annotation { "Feature Type Name" : "Feature", "Feature Type Description" : "" }
export const myFeature = defineFeature(function(context is Context, id is Id, definition is map)
    precondition{}
    {
        {
            var Q0;
            Q0=qCreatedBy(makeId("Right.planeOp"),FACE);
            var sketch = newSketch(context, id + "F0", { "sketchPlane" : qUnion([Q0])});
            skLineSegment(sketch, "E0", {"start": v(0, 0) * mm, "end": v(-381, 0) * mm});
            skLineSegment(sketch, "E1", {"start": v(0, 0) * mm, "end": v(381, 0) * mm});
            skLineSegment(sketch, "E2", {"start": v(0, 0) * mm, "end": v(0, 190.5) * mm});
            skLineSegment(sketch, "E3", {"start": v(0, 190.5) * mm, "end": v(0, 228.6) * mm});
            skLineSegment(sketch, "E4", {"start": v(381, 0) * mm, "end": v(457.2, 0) * mm});
            skLineSegment(sketch, "E5", {"start": v(-381, 0) * mm, "end": v(-457.2, 0) * mm});
            skLineSegment(sketch, "E6", {"start": v(-457.2, 0) * mm, "end": v(0, 228.6) * mm});
            skLineSegment(sketch, "E7", {"start": v(457.2, 0) * mm, "end": v(0, 228.6) * mm});
            skLineSegment(sketch, "E8", {"start": v(381, 0) * mm, "end": v(0, 190.5) * mm});
            skLineSegment(sketch, "E9", {"start": v(-381, 0) * mm, "end": v(0, 190.5) * mm});
            skLineSegment(sketch, "E10", {"start": v(-381, 0) * mm, "end": v(-381, -279.4) * mm});
            skLineSegment(sketch, "E11", {"start": v(-381, -279.4) * mm, "end": v(-381, -330.2) * mm});
            skLineSegment(sketch, "E12", {"start": v(381, 0) * mm, "end": v(381, -279.4) * mm});
            skLineSegment(sketch, "E13", {"start": v(-381, -279.4) * mm, "end": v(381, -279.4) * mm});
            skLineSegment(sketch, "E14", {"start": v(381, -279.4) * mm, "end": v(381, -330.2) * mm});
            skLineSegment(sketch, "E15", {"start": v(381, -330.2) * mm, "end": v(-381, -330.2) * mm});
            skLineSegment(sketch, "E16", {"start": v(381, -279.4) * mm, "end": v(762, -279.4) * mm});
            skLineSegment(sketch, "E17", {"start": v(381, -330.2) * mm, "end": v(762, -330.2) * mm});
            skLineSegment(sketch, "E18", {"start": v(762, -330.2) * mm, "end": v(762, -279.4) * mm});
            skLineSegment(sketch, "E19", {"start": v(762, -279.4) * mm, "end": v(762, -50.8) * mm});
            skLineSegment(sketch, "E20", {"start": v(381, 0) * mm, "end": v(762, -50.8) * mm});
            skLineSegment(sketch, "E21", {"start": v(381, 0) * mm, "end": v(381, -50.8) * mm});
            skLineSegment(sketch, "E22", {"start": v(762, -50.8) * mm, "end": v(762, -101.6) * mm});
            skLineSegment(sketch, "E23", {"start": v(762, -101.6) * mm, "end": v(381, -50.8) * mm});
            skLineSegment(sketch, "E24", {"start": v(-279.4, -279.4) * mm, "end": v(-279.4, -101.6) * mm});
            skLineSegment(sketch, "E25", {"start": v(-279.4, -101.6) * mm, "end": v(-203.2, -101.6) * mm});
            skLineSegment(sketch, "E26", {"start": v(-203.2, -101.6) * mm, "end": v(-203.2, -279.4) * mm});
            skLineSegment(sketch, "E27.bottom", {"start": v(50.8, -101.6) * mm, "end": v(279.4, -101.6) * mm});
            skLineSegment(sketch, "E27.top", {"start": v(50.8, -203.2) * mm, "end": v(279.4, -203.2) * mm});
            skLineSegment(sketch, "E27.left", {"start": v(50.8, -101.6) * mm, "end": v(50.8, -203.2) * mm});
            skLineSegment(sketch, "E27.right", {"start": v(279.4, -101.6) * mm, "end": v(279.4, -203.2) * mm});
            skLineSegment(sketch, "E28.0", {"start": v(63.5, -190.5) * mm, "end": v(266.7, -190.5) * mm});
            skLineSegment(sketch, "E28.1", {"start": v(63.5, -114.3) * mm, "end": v(63.5, -190.5) * mm});
            skLineSegment(sketch, "E28.2", {"start": v(63.5, -114.3) * mm, "end": v(266.7, -114.3) * mm});
            skLineSegment(sketch, "E28.3", {"start": v(266.7, -114.3) * mm, "end": v(266.7, -190.5) * mm});
            skLineSegment(sketch, "E29.0", {"start": v(-177.8, -76.2) * mm, "end": v(-177.8, -279.4) * mm});
            skLineSegment(sketch, "E29.1", {"start": v(-304.8, -76.2) * mm, "end": v(-177.8, -76.2) * mm});
            skLineSegment(sketch, "E29.2", {"start": v(-304.8, -279.4) * mm, "end": v(-304.8, -76.2) * mm});
            skLineSegment(sketch, "E30.bottom", {"start": v(533.4, -122.37) * mm, "end": v(635, -122.37) * mm});
            skLineSegment(sketch, "E30.top", {"start": v(533.4, -223.97) * mm, "end": v(635, -223.97) * mm});
            skLineSegment(sketch, "E30.left", {"start": v(533.4, -122.37) * mm, "end": v(533.4, -223.97) * mm});
            skLineSegment(sketch, "E30.right", {"start": v(635, -122.37) * mm, "end": v(635, -223.97) * mm});
            skLineSegment(sketch, "E31.0", {"start": v(515.62, -104.59) * mm, "end": v(652.78, -104.59) * mm});
            skLineSegment(sketch, "E31.1", {"start": v(515.62, -104.59) * mm, "end": v(515.62, -241.75) * mm});
            skLineSegment(sketch, "E31.2", {"start": v(515.62, -241.75) * mm, "end": v(652.78, -241.75) * mm});
            skLineSegment(sketch, "E31.3", {"start": v(652.78, -104.59) * mm, "end": v(652.78, -241.75) * mm});
            skText(sketch, "E32", { "text": "Blake Carey\n", "fontName": "OpenSans-Bold.ttf"});
            const initialGuessF0  = {"E32": [-0.79069, -0.70956, 1, 0, 0.20028]};
            skSetInitialGuess(sketch, initialGuessF0);
            skSolve(sketch);
        }
        {
            var Q0;
            Q0=makeQuery(id+"F0.imprint","IMPRINT",FACE,{"disambiguationData":[TD([[makeQuery(id+"F0.imprint","IMPRINT",EDGE,{"derivedFrom":sQuery(id+"F0.wireOp",EDGE,"E0")}),-1.0]])]});
            var Q1;
            Q1=makeQuery(id+"F0.imprint","IMPRINT",FACE,{"disambiguationData":[TD([[makeQuery(id+"F0.imprint","IMPRINT",EDGE,{"derivedFrom":sQuery(id+"F0.wireOp",EDGE,"E1")}),1.0]])]});
            var Q2;
            Q2=makeQuery(id+"F0.imprint","IMPRINT",FACE,{"disambiguationData":[TD([[makeQuery(id+"F0.imprint","IMPRINT",EDGE,{"derivedFrom":sQuery(id+"F0.wireOp",EDGE,"E0")}),1.0]])]});
            var Q3;
            Q3=makeQuery(id+"F0.imprint","IMPRINT",FACE,{"disambiguationData":[TD([[makeQuery(id+"F0.imprint","IMPRINT",EDGE,{"derivedFrom":sQuery(id+"F0.wireOp",EDGE,"E12")}),1.0]])]});
            var Q4;
            {var subQ4=sQuery(id+"F0.wireOp",EDGE,"E11");Q4=makeQuery(id+"F0.imprint","IMPRINT",FACE,{"disambiguationData":[TD([[makeQuery(id+"F0.imprint","IMPRINT",EDGE,{"derivedFrom":subQ4}),1.0]])]});}
            var Q5;
            Q5=makeQuery(id+"F0.imprint","IMPRINT",FACE,{"disambiguationData":[TD([[makeQuery(id+"F0.imprint","IMPRINT",EDGE,{"derivedFrom":sQuery(id+"F0.wireOp",EDGE,"E14")}),1.0]])]});
            extrude(context, id + "F1", {"entities" : qUnion([Q0, Q1, Q2, Q3, Q4, Q5]), "endBound" : BoundingType.SYMMETRIC, "depth" : 1016 * mm, "offsetDistance" : 25.4 * mm});
        }
        {
            var Q0;
            Q0=makeQuery(id+"F0.imprint","IMPRINT",FACE,{"disambiguationData":[TD([[makeQuery(id+"F0.imprint","IMPRINT",EDGE,{"derivedFrom":sQuery(id+"F0.wireOp",EDGE,"E3")}),1.0]])]});
            var Q1;
            Q1=makeQuery(id+"F0.imprint","IMPRINT",FACE,{"disambiguationData":[TD([[makeQuery(id+"F0.imprint","IMPRINT",EDGE,{"derivedFrom":sQuery(id+"F0.wireOp",EDGE,"E3")}),-1.0]])]});
            extrude(context, id + "F2", {"entities" : qUnion([Q0, Q1]), "operationType" : NewBodyOperationType.ADD, "depth" : 533.4 * mm, "offsetDistance" : 25.4 * mm});
        }
        {
            var Q0;
            Q0=makeQuery(id+"F0.imprint","IMPRINT",FACE,{"disambiguationData":[TD([[makeQuery(id+"F0.imprint","IMPRINT",EDGE,{"derivedFrom":sQuery(id+"F0.wireOp",EDGE,"E28.0")}),1.0]])]});
            var Q1;
            Q1=makeQuery(id+"F0.imprint","IMPRINT",FACE,{"disambiguationData":[TD([[makeQuery(id+"F0.imprint","IMPRINT",EDGE,{"derivedFrom":sQuery(id+"F0.wireOp",EDGE,"E30.bottom")}),-1.0]])]});
            extrude(context, id + "F3", {"entities" : qUnion([Q0, Q1]), "depth" : 520.7 * mm, "offsetDistance" : 25.4 * mm});
        }
        {
            var Q0;
            Q0=makeQuery(id+"F1.opExtrude","SWEPT_FACE",FACE,{"disambiguationData":[OSD([sQuery(id+"F0.wireOp",EDGE,"E10"),sQuery(id+"F0.wireOp",EDGE,"E11")])]});
            var sketch = newSketch(context, id + "F4", { "sketchPlane" : qUnion([Q0])});
            skLineSegment(sketch, "E33.bottom", {"start": v(-354.94, -82.37) * mm, "end": v(-227.94, -82.37) * mm});
            skLineSegment(sketch, "E33.top", {"start": v(-354.94, -183.97) * mm, "end": v(-227.94, -183.97) * mm});
            skLineSegment(sketch, "E33.left", {"start": v(-354.94, -82.37) * mm, "end": v(-354.94, -183.97) * mm});
            skLineSegment(sketch, "E33.right", {"start": v(-227.94, -82.37) * mm, "end": v(-227.94, -183.97) * mm});
            skLineSegment(sketch, "E34.bottom", {"start": v(112.52, -104.92) * mm, "end": v(366.52, -104.92) * mm});
            skLineSegment(sketch, "E34.top", {"start": v(112.52, -257.32) * mm, "end": v(366.52, -257.32) * mm});
            skLineSegment(sketch, "E34.left", {"start": v(112.52, -104.92) * mm, "end": v(112.52, -257.32) * mm});
            skLineSegment(sketch, "E34.right", {"start": v(366.52, -104.92) * mm, "end": v(366.52, -257.32) * mm});
            skLineSegment(sketch, "E35.0", {"start": v(-367.64, -69.67) * mm, "end": v(-215.24, -69.67) * mm});
            skLineSegment(sketch, "E35.1", {"start": v(-367.64, -69.67) * mm, "end": v(-367.64, -196.67) * mm});
            skLineSegment(sketch, "E35.2", {"start": v(-367.64, -196.67) * mm, "end": v(-215.24, -196.67) * mm});
            skLineSegment(sketch, "E35.3", {"start": v(-215.24, -69.67) * mm, "end": v(-215.24, -196.67) * mm});
            skLineSegment(sketch, "E36.0", {"start": v(99.82, -92.22) * mm, "end": v(379.22, -92.22) * mm});
            skLineSegment(sketch, "E36.1", {"start": v(99.82, -92.22) * mm, "end": v(99.82, -270.02) * mm});
            skLineSegment(sketch, "E36.2", {"start": v(99.82, -270.02) * mm, "end": v(379.22, -270.02) * mm});
            skLineSegment(sketch, "E36.3", {"start": v(379.22, -92.22) * mm, "end": v(379.22, -270.02) * mm});
            skSolve(sketch);
        }
        {
            var Q0;
            Q0=makeQuery(id+"F4.imprint","IMPRINT",FACE,{"disambiguationData":[TD([[makeQuery(id+"F4.imprint","IMPRINT",EDGE,{"derivedFrom":sQuery(id+"F4.wireOp",EDGE,"E33.bottom")}),-1.0]])]});
            var Q1;
            Q1=makeQuery(id+"F4.imprint","IMPRINT",FACE,{"disambiguationData":[TD([[makeQuery(id+"F4.imprint","IMPRINT",EDGE,{"derivedFrom":sQuery(id+"F4.wireOp",EDGE,"E34.bottom")}),-1.0]])]});
            extrude(context, id + "F5", {"entities" : qUnion([Q0, Q1]), "operationType" : NewBodyOperationType.ADD, "depth" : 12.7 * mm, "offsetDistance" : 25.4 * mm});
        }
        {
            var Q0;
            Q0=qCreatedBy(makeId("Right.planeOp"),FACE);
            var sketch = newSketch(context, id + "F6", { "sketchPlane" : qUnion([Q0])});
            skText(sketch, "E37", { "text": "Blake Carey", "fontName": "OpenSans-Bold.ttf"});
            const initialGuessF6  = {"E37": [-0.99379, -0.62626, 1, 0, 0.17761]};
            skSetInitialGuess(sketch, initialGuessF6);
            skSolve(sketch);
        }
        {
            var Q0;
            Q0 = qSketchRegion(id + "F6", true);
            extrude(context, id + "F7", {"entities" : qUnion([Q0]), "depth" : 508 * mm, "offsetDistance" : 25.4 * mm});
        }
        {
            var Q0;
            {var subQ0=sQuery(id+"F0.wireOp",EDGE,"E24");Q0=makeQuery(id+"F0.imprint","IMPRINT",FACE,{"disambiguationData":[TD([[makeQuery(id+"F0.imprint","IMPRINT",EDGE,{"derivedFrom":subQ0}),-1.0]])]});}
            var Q1;
            Q1=makeQuery(id+"F7.opExtrude","CAP_FACE",FACE,{"disambiguationData":[OSD([sQuery(id+"F6.wireOp",EDGE,"E37.sketch_text.stroke-0"),sQuery(id+"F6.wireOp",EDGE,"E37.sketch_text.stroke-1"),sQuery(id+"F6.wireOp",EDGE,"E37.sketch_text.stroke-2"),sQuery(id+"F6.wireOp",EDGE,"E37.sketch_text.stroke-3"),sQuery(id+"F6.wireOp",EDGE,"E37.sketch_text.stroke-4"),sQuery(id+"F6.wireOp",EDGE,"E37.sketch_text.stroke-5"),sQuery(id+"F6.wireOp",EDGE,"E37.sketch_text.stroke-6"),sQuery(id+"F6.wireOp",EDGE,"E37.sketch_text.stroke-7"),sQuery(id+"F6.wireOp",EDGE,"E37.sketch_text.stroke-8"),sQuery(id+"F6.wireOp",EDGE,"E37.sketch_text.stroke-9"),sQuery(id+"F6.wireOp",EDGE,"E37.sketch_text.stroke-10"),sQuery(id+"F6.wireOp",EDGE,"E37.sketch_text.stroke-11"),sQuery(id+"F6.wireOp",EDGE,"E37.sketch_text.stroke-12"),sQuery(id+"F6.wireOp",EDGE,"E37.sketch_text.stroke-13"),sQuery(id+"F6.wireOp",EDGE,"E37.sketch_text.stroke-14"),sQuery(id+"F6.wireOp",EDGE,"E37.sketch_text.stroke-15"),sQuery(id+"F6.wireOp",EDGE,"E37.sketch_text.stroke-16"),sQuery(id+"F6.wireOp",EDGE,"E37.sketch_text.stroke-17"),sQuery(id+"F6.wireOp",EDGE,"E37.sketch_text.stroke-18"),sQuery(id+"F6.wireOp",EDGE,"E37.sketch_text.stroke-19"),sQuery(id+"F6.wireOp",EDGE,"E37.sketch_text.stroke-20"),sQuery(id+"F6.wireOp",EDGE,"E37.sketch_text.stroke-21"),sQuery(id+"F6.wireOp",EDGE,"E37.sketch_text.stroke-22"),sQuery(id+"F6.wireOp",EDGE,"E37.sketch_text.stroke-23"),sQuery(id+"F6.wireOp",EDGE,"E37.sketch_text.stroke-24")])],"isStart":false});
            extrude(context, id + "F8", {"entities" : qUnion([Q0, Q1]), "operationType" : NewBodyOperationType.ADD, "depth" : -12.7 * mm, "offsetDistance" : 25.4 * mm});
        }
    });